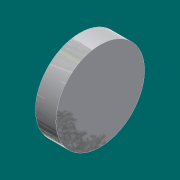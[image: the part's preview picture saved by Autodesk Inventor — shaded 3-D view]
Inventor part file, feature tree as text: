
AUTODESK INVENTOR PART (.ipt)
format: ipt  version: 2017 (Build 210142000, 142)  size: 200,704 bytes
history: native  units: mm (DEFAULTED — no unit token found)
features: other x4, revolve x1, sketch x1
ambient origin geometry x8: Origin, YZ Plane, XZ Plane, XY Plane, X Axis, Y Axis, Z Axis, Center Point
bodies: Solid1 (feature_tree)
feature tree (6):
  revolve  "Revolve1"  [1 undecoded]
  other  "Work Axis1"
  other  "Work Point1"
  other  "Work Point2"
  other  "Work Point3"
  sketch  "Sketch1"  dims[d4=90.0deg d0=73.8124mm d1=7.6708mm d2=15.748mm d3=4.826mm]
note: 1 required parameter value undecoded (feature->parameter linkage not recoverable at this tier; creation-order binding heuristic only, values carry confidence <= 0.55)
